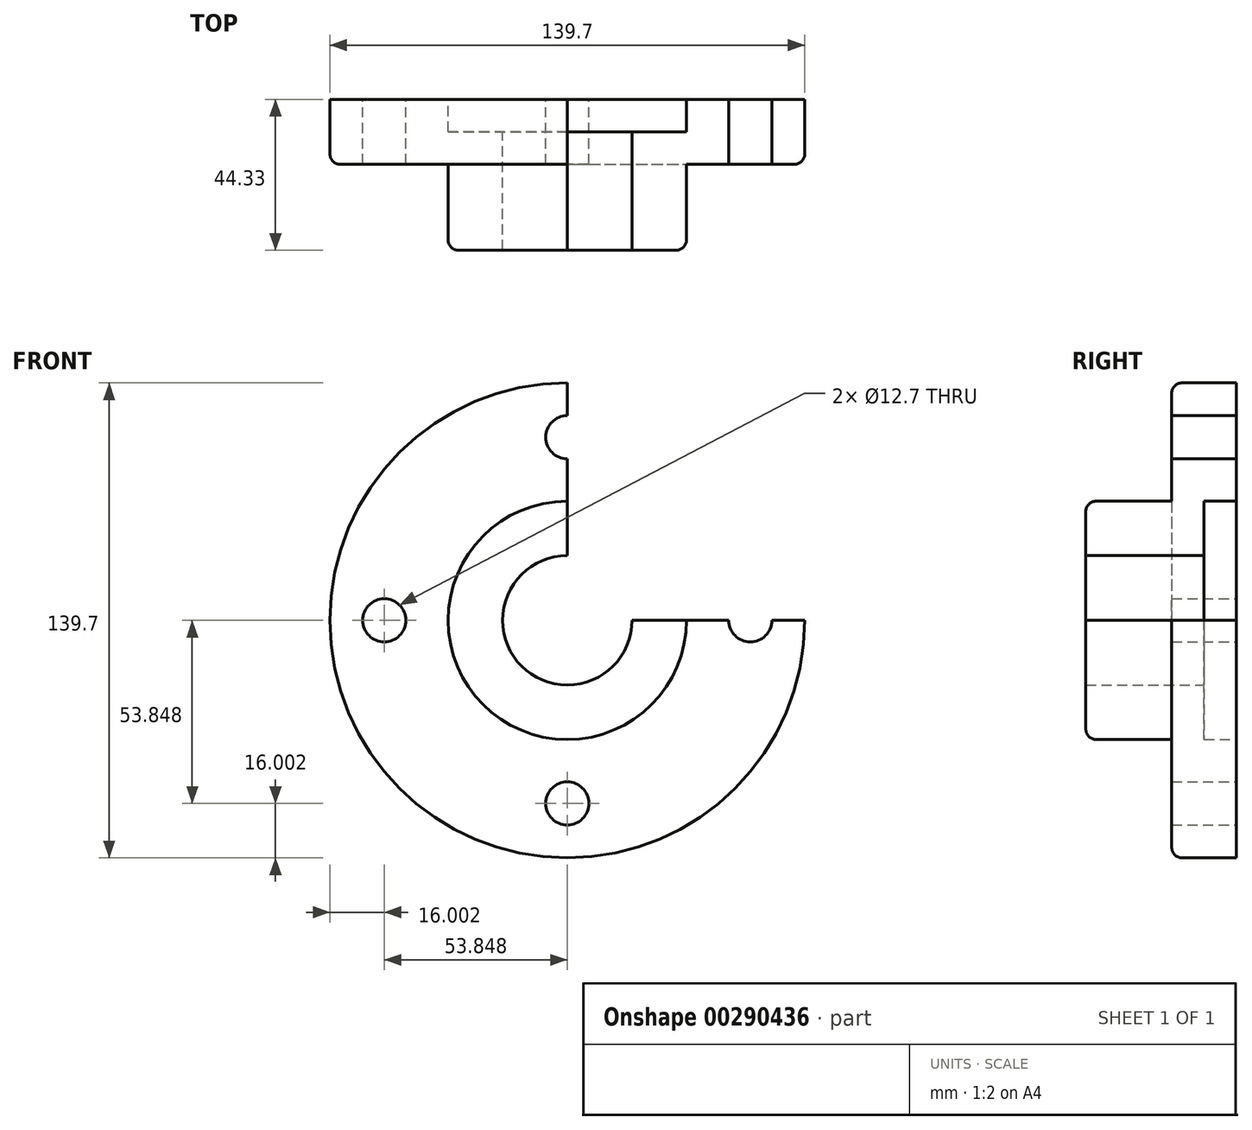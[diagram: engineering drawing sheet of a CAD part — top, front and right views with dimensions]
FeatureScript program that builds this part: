
annotation { "Feature Type Name" : "Feature", "Feature Type Description" : "" }
export const myFeature = defineFeature(function(context is Context, id is Id, definition is map)
    precondition{}
    {
        {
            var Q0;
            Q0=qCreatedBy(makeId("Front.planeOp"),FACE);
            var sketch = newSketch(context, id + "F0", { "sketchPlane" : qUnion([Q0])});
            skCircle(sketch, "E0", {"center": v(0, 0) * mm, "radius": 19.05 * mm});
            skCircle(sketch, "E1", {"center": v(0, 0) * mm, "radius": 35.05 * mm});
            skCircle(sketch, "E2", {"center": v(53.85, 0) * mm, "radius": 6.35 * mm});
            skCircle(sketch, "E3", {"center": v(-53.85, 0) * mm, "radius": 6.35 * mm});
            skCircle(sketch, "E4", {"center": v(0, 0) * mm, "radius": 69.85 * mm});
            skCircle(sketch, "E5", {"center": v(0, 53.85) * mm, "radius": 6.35 * mm});
            skCircle(sketch, "E6", {"center": v(0, -53.85) * mm, "radius": 6.35 * mm});
            skCircle(sketch, "E7", {"center": v(0, 0) * mm, "radius": 53.85 * mm});
            skSolve(sketch);
        }
        {
            var Q0;
            Q0=qCreatedBy(makeId("Front.planeOp"),FACE);
            var sketch = newSketch(context, id + "F1", { "sketchPlane" : qUnion([Q0])});
            skCircle(sketch, "E8", {"center": v(0, 0) * mm, "radius": 35.05 * mm});
            skCircle(sketch, "E9", {"center": v(0, 0) * mm, "radius": 19.05 * mm});
            skSolve(sketch);
        }
        {
            var Q0;
            Q0=makeQuery(id+"F0.imprint","IMPRINT",FACE,{"disambiguationData":[TD([[makeQuery(id+"F0.imprint","IMPRINT",EDGE,{"derivedFrom":sQuery(id+"F0.wireOp",EDGE,"E1")}),-1.0]])]});
            var Q1;
            Q1=makeQuery(id+"F0.imprint","IMPRINT",FACE,{"disambiguationData":[TD([[makeQuery(id+"F0.imprint","IMPRINT",EDGE,{"derivedFrom":sQuery(id+"F0.wireOp",EDGE,"E4")}),1.0]])]});
            extrude(context, id + "F2", {"entities" : qUnion([Q0, Q1]), "endBound" : BoundingType.SYMMETRIC, "depth" : 19.05 * mm});
        }
        {
            var Q0;
            Q0=makeQuery(id+"F1.imprint","IMPRINT",FACE,{"disambiguationData":[TD([[makeQuery(id+"F1.imprint","IMPRINT",EDGE,{"derivedFrom":sQuery(id+"F1.wireOp",EDGE,"E8")}),1.0]])]});
            extrude(context, id + "F3", {"entities" : qUnion([Q0]), "operationType" : NewBodyOperationType.ADD, "depth" : 34.8 * mm});
        }
        {
            var Q0;
            Q0=makeQuery(id+"F2.opExtrude","CAP_EDGE",EDGE,{"disambiguationData":[OSD([sQuery(id+"F0.wireOp",EDGE,"E1")])],"isStart":false});
            var Q1;
            Q1=makeQuery(id+"F3.opExtrude","CAP_EDGE",EDGE,{"disambiguationData":[OSD([sQuery(id+"F1.wireOp",EDGE,"E8")])],"isStart":false});
            var Q2;
            Q2=makeQuery(id+"F2.opExtrude","CAP_EDGE",EDGE,{"disambiguationData":[OSD([sQuery(id+"F0.wireOp",EDGE,"E4")])],"isStart":false});
            fillet(context, id + "F4", {"entities" : qUnion([Q0, Q1, Q2]), "radius" : 3.05 * mm, "tangentPropagation" : true, "allowEdgeOverflow" : false});
        }
        {
            var Q0;
            Q0=qCreatedBy(makeId("Front.planeOp"),FACE);
            var sketch = newSketch(context, id + "F5", { "sketchPlane" : qUnion([Q0])});
            skLineSegment(sketch, "E10", {"start": v(0, 76.32) * mm, "end": v(0, 0) * mm});
            skLineSegment(sketch, "E11", {"start": v(0, 0) * mm, "end": v(76.14, 0) * mm});
            skLineSegment(sketch, "E12", {"start": v(76.14, 0) * mm, "end": v(76.14, 76.14) * mm});
            skLineSegment(sketch, "E13", {"start": v(76.14, 76.14) * mm, "end": v(0, 76.32) * mm});
            skSolve(sketch);
        }
        {
            var Q0;
            Q0 = qSketchRegion(id + "F5", true);
            extrude(context, id + "F6", {"entities" : qUnion([Q0]), "operationType" : NewBodyOperationType.REMOVE, "endBound" : BoundingType.THROUGH_ALL, "depth" : 60.2 * mm});
        }
        {
            var Q0;
            Q0=qCreatedBy(makeId("Front.planeOp"),FACE);
            var sketch = newSketch(context, id + "F7", { "sketchPlane" : qUnion([Q0])});
            skLineSegment(sketch, "E14", {"start": v(0, 76.14) * mm, "end": v(0, 0) * mm});
            skLineSegment(sketch, "E15", {"start": v(0, 0) * mm, "end": v(76.7, 0) * mm});
            skLineSegment(sketch, "E16", {"start": v(76.7, 0) * mm, "end": v(76.7, 76.32) * mm});
            skLineSegment(sketch, "E17", {"start": v(76.7, 76.32) * mm, "end": v(0, 76.14) * mm});
            skSolve(sketch);
        }
        {
            var Q0;
            Q0 = qSketchRegion(id + "F7", true);
            extrude(context, id + "F8", {"entities" : qUnion([Q0]), "operationType" : NewBodyOperationType.REMOVE, "endBound" : BoundingType.THROUGH_ALL, "oppositeDirection" : true, "depth" : 52.58 * mm});
        }
    });
